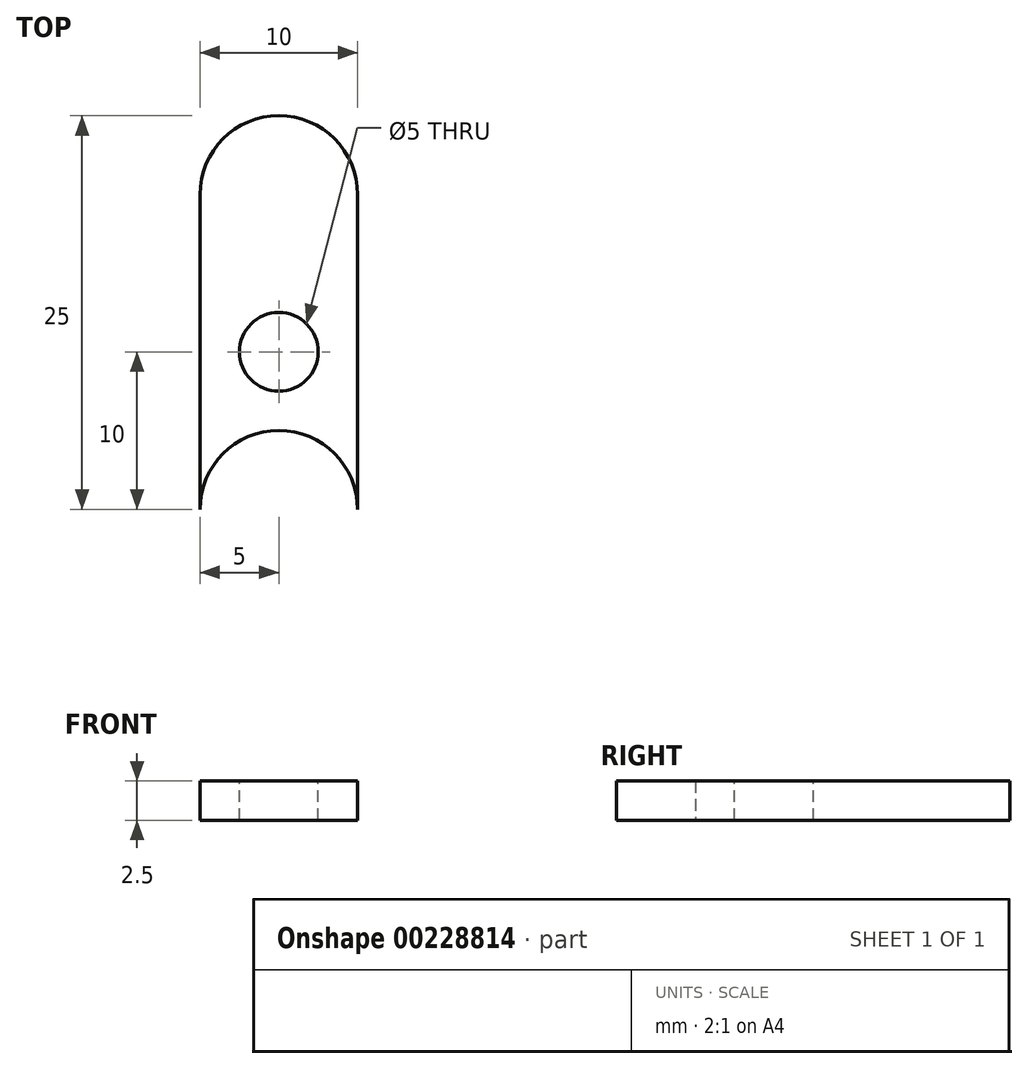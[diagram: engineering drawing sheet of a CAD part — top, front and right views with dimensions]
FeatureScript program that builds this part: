
annotation { "Feature Type Name" : "Feature", "Feature Type Description" : "" }
export const myFeature = defineFeature(function(context is Context, id is Id, definition is map)
    precondition{}
    {
        {
            var Q0;
            Q0=qCreatedBy(makeId("Top.planeOp"),FACE);
            var sketch = newSketch(context, id + "F0", { "sketchPlane" : qUnion([Q0])});
            skLineSegment(sketch, "E0.top", {"start": v(-5, 0) * mm, "end": v(5, 0) * mm});
            skLineSegment(sketch, "E0.left", {"start": v(-5, 10) * mm, "end": v(-5, 0) * mm});
            skLineSegment(sketch, "E0.right", {"start": v(5, 10) * mm, "end": v(5, 0) * mm});
            skCircle(sketch, "E1", {"center": v(0, 10) * mm, "radius": 5 * mm});
            skLineSegment(sketch, "E2.MirrorCS", {"start": v(-5, -10) * mm, "end": v(-5, 0) * mm});
            skLineSegment(sketch, "E3.MirrorCS", {"start": v(5, -10) * mm, "end": v(5, 0) * mm});
            skCircle(sketch, "E4.MirrorC", {"center": v(0, -10) * mm, "radius": 5 * mm});
            skSolve(sketch);
        }
        {
            var Q0;
            {var subQ0=sQuery(id+"F0.wireOp",EDGE,"E0.bottom");Q0=makeQuery(id+"F0.imprint","IMPRINT",FACE,{"disambiguationData":[TD([[makeQuery(id+"F0.imprint","IMPRINT",EDGE,{"derivedFrom":subQ0}),1.0]])]});}
            var Q1;
            {var subQ0=sQuery(id+"F0.wireOp",EDGE,"E0.bottom");Q1=makeQuery(id+"F0.imprint","IMPRINT",FACE,{"disambiguationData":[TD([[makeQuery(id+"F0.imprint","IMPRINT",EDGE,{"derivedFrom":subQ0}),-1.0]])]});}
            var Q2;
            {var subQ0=sQuery(id+"F0.wireOp",EDGE,"E0.left");Q2=makeQuery(id+"F0.imprint","IMPRINT",FACE,{"disambiguationData":[TD([[makeQuery(id+"F0.imprint","IMPRINT",EDGE,{"derivedFrom":subQ0}),1.0]])]});}
            var Q3;
            Q3=makeQuery(id+"F0.imprint","IMPRINT",FACE,{"disambiguationData":[TD([[makeQuery(id+"F0.imprint","IMPRINT",EDGE,{"derivedFrom":sQuery(id+"F0.wireOp",EDGE,"E0.top")}),-1.0]])]});
            var Q4;
            {var subQ0=sQuery(id+"F0.wireOp",EDGE,"abf55d34-d809-4182-a846-678f96c4c0e90.MirrorCS");Q4=makeQuery(id+"F0.imprint","IMPRINT",FACE,{"disambiguationData":[TD([[makeQuery(id+"F0.imprint","IMPRINT",EDGE,{"derivedFrom":subQ0}),1.0]])]});}
            var Q5;
            {var subQ0=sQuery(id+"F0.wireOp",EDGE,"abf55d34-d809-4182-a846-678f96c4c0e90.MirrorCS");Q5=makeQuery(id+"F0.imprint","IMPRINT",FACE,{"disambiguationData":[TD([[makeQuery(id+"F0.imprint","IMPRINT",EDGE,{"derivedFrom":subQ0}),-1.0]])]});}
            var Q6;
            {var subQ0=sQuery(id+"F0.wireOp",EDGE,"E1");var subQ1=makeQuery(id+"F0.imprint","INTERSECT",VERTEX,{"derivedFrom":[sQuery(id+"F0.wireOp",EDGE,"E0.left"),subQ0]});Q6=makeQuery(id+"F0.imprint","IMPRINT",FACE,{"disambiguationData":[TD([[makeQuery(id+"F0.imprint","IMPRINT",EDGE,{"disambiguationData":[TD([[subQ1,1.0]])],"derivedFrom":subQ0}),1.0]])]});}
            var Q7;
            {var subQ0=sQuery(id+"F0.wireOp",EDGE,"E4.MirrorC");var subQ1=makeQuery(id+"F0.imprint","INTERSECT",VERTEX,{"derivedFrom":[sQuery(id+"F0.wireOp",EDGE,"E2.MirrorCS"),subQ0]});Q7=makeQuery(id+"F0.imprint","IMPRINT",FACE,{"disambiguationData":[TD([[makeQuery(id+"F0.imprint","IMPRINT",EDGE,{"disambiguationData":[TD([[subQ1,1.0]])],"derivedFrom":subQ0}),-1.0]])]});}
            extrude(context, id + "F1", {"entities" : qUnion([Q0, Q1, Q2, Q3, Q4, Q5, Q6, Q7]), "endBound" : BoundingType.SYMMETRIC, "depth" : 2.5 * mm});
        }
        {
            var Q0;
            Q0=makeQuery(id+"F1.opExtrude","CAP_FACE",FACE,{"disambiguationData":[OSD([sQuery(id+"F0.wireOp",EDGE,"E0.left"),sQuery(id+"F0.wireOp",EDGE,"E0.right"),sQuery(id+"F0.wireOp",EDGE,"E1"),sQuery(id+"F0.wireOp",EDGE,"E2.MirrorCS"),sQuery(id+"F0.wireOp",EDGE,"E3.MirrorCS"),sQuery(id+"F0.wireOp",EDGE,"E4.MirrorC")])],"isStart":false});
            var sketch = newSketch(context, id + "F2", { "sketchPlane" : qUnion([Q0])});
            skCircle(sketch, "E5", {"center": v(0, 0) * mm, "radius": 2.5 * mm});
            skSolve(sketch);
        }
        {
            var Q0;
            Q0=makeQuery(id+"F2.imprint","IMPRINT",FACE,{"disambiguationData":[TD([[makeQuery(id+"F2.imprint","IMPRINT",EDGE,{"derivedFrom":sQuery(id+"F2.wireOp",EDGE,"E5")}),1.0]])]});
            extrude(context, id + "F3", {"entities" : qUnion([Q0]), "operationType" : NewBodyOperationType.REMOVE, "endBound" : BoundingType.THROUGH_ALL, "oppositeDirection" : true, "depth" : 25 * mm});
        }
    });
